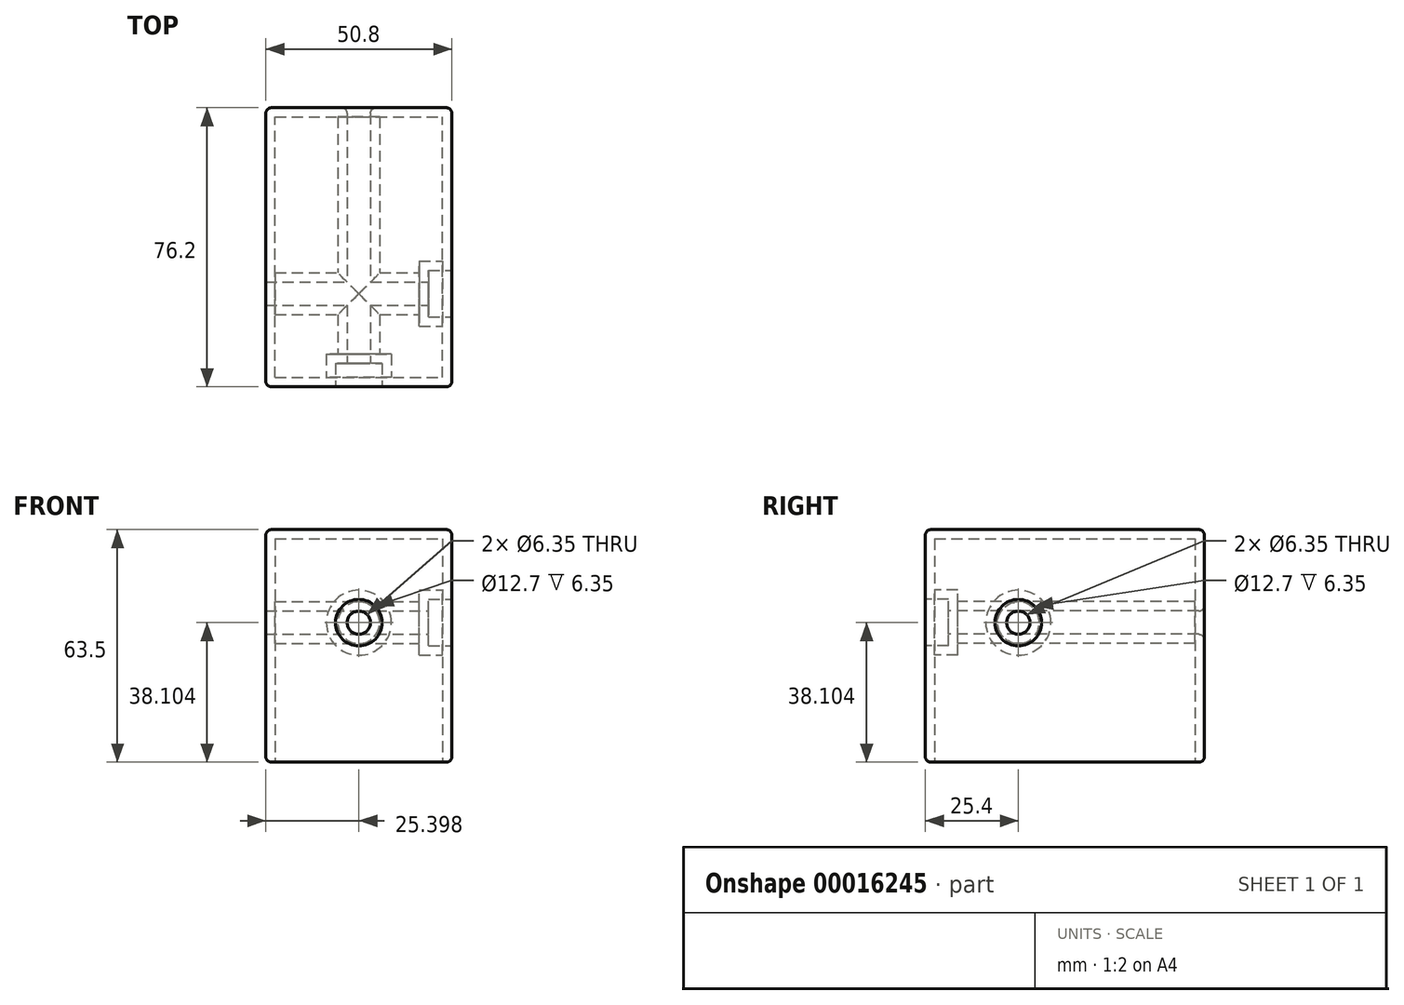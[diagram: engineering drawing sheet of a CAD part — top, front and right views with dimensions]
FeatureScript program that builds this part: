
annotation { "Feature Type Name" : "Feature", "Feature Type Description" : "" }
export const myFeature = defineFeature(function(context is Context, id is Id, definition is map)
    precondition{}
    {
        {
            var Q0;
            Q0=qCreatedBy(makeId("Front.planeOp"),FACE);
            var sketch = newSketch(context, id + "F0", { "sketchPlane" : qUnion([Q0])});
            skLineSegment(sketch, "E0.bottom", {"start": v(-45.47, 53.6) * mm, "end": v(5.33, 53.6) * mm});
            skLineSegment(sketch, "E0.top", {"start": v(-45.47, -9.9) * mm, "end": v(5.33, -9.9) * mm});
            skLineSegment(sketch, "E0.left", {"start": v(-45.47, 53.6) * mm, "end": v(-45.47, -9.9) * mm});
            skLineSegment(sketch, "E0.right", {"start": v(5.33, 53.6) * mm, "end": v(5.33, -9.9) * mm});
            skSolve(sketch);
        }
        {
            var Q0;
            Q0=makeQuery(id+"F0.imprint","IMPRINT",FACE,{"disambiguationData":[TD([[makeQuery(id+"F0.imprint","IMPRINT",EDGE,{"derivedFrom":sQuery(id+"F0.wireOp",EDGE,"E0.bottom")}),-1.0]])]});
            extrude(context, id + "F1", {"entities" : qUnion([Q0]), "depth" : 76.2 * mm});
        }
        {
            var Q0;
            Q0=makeQuery(id+"F1.opExtrude","CAP_FACE",FACE,{"disambiguationData":[OSD([sQuery(id+"F0.wireOp",EDGE,"E0.bottom"),sQuery(id+"F0.wireOp",EDGE,"E0.top"),sQuery(id+"F0.wireOp",EDGE,"E0.left"),sQuery(id+"F0.wireOp",EDGE,"E0.right")])],"isStart":false});
            var sketch = newSketch(context, id + "F2", { "sketchPlane" : qUnion([Q0])});
            skPoint(sketch, "E1", {"position": v(-20.07, 28.2) * mm});
            skSolve(sketch);
        }
        {
            var Q0;
            Q0=sQuery(id+"F2.wireOp",VERTEX,"E1");
            var Q1;
            Q1=makeQuery(id+"F1.opExtrude","SWEPT_BODY",BODY,{"disambiguationData":[OSD([sQuery(id+"F0.wireOp",EDGE,"E0.bottom"),sQuery(id+"F0.wireOp",EDGE,"E0.top"),sQuery(id+"F0.wireOp",EDGE,"E0.left"),sQuery(id+"F0.wireOp",EDGE,"E0.right")])]});
            hole(context, id + "F3", {"style" : HoleStyle.C_BORE, "holeDiameter" : 6.35 * mm, "cBoreDiameter" : 12.7 * mm, "cBoreDepth" : 6.35 * mm, "endStyle" : HoleEndStyle.THROUGH, "locations" : qUnion([Q0]), "scope" : qUnion([Q1])});
        }
        {
            var Q0;
            Q0=makeQuery(id+"F1.opExtrude","SWEPT_FACE",FACE,{"disambiguationData":[OSD([sQuery(id+"F0.wireOp",EDGE,"E0.right")])]});
            var sketch = newSketch(context, id + "F4", { "sketchPlane" : qUnion([Q0])});
            skCircle(sketch, "E2", {"center": v(-50.8, 28.2) * mm, "radius": 7.94 * mm});
            skSolve(sketch);
        }
        {
            var Q0;
            Q0=sQuery(id+"F4.wireOp",VERTEX,"E2.center");
            var Q1;
            Q1=makeQuery(id+"F1.opExtrude","SWEPT_BODY",BODY,{"disambiguationData":[OSD([sQuery(id+"F0.wireOp",EDGE,"E0.bottom"),sQuery(id+"F0.wireOp",EDGE,"E0.top"),sQuery(id+"F0.wireOp",EDGE,"E0.left"),sQuery(id+"F0.wireOp",EDGE,"E0.right")])]});
            hole(context, id + "F5", {"style" : HoleStyle.C_BORE, "holeDiameter" : 6.35 * mm, "cBoreDiameter" : 12.7 * mm, "cBoreDepth" : 6.35 * mm, "endStyle" : HoleEndStyle.THROUGH, "locations" : qUnion([Q0]), "scope" : qUnion([Q1])});
        }
        {
            var Q0;
            Q0=makeQuery(id+"F1.opExtrude","SWEPT_FACE",FACE,{"disambiguationData":[OSD([sQuery(id+"F0.wireOp",EDGE,"E0.top")])]});
            shell(context, id + "F6", {"entities" : qUnion([Q0]), "thickness" : 2.54 * mm});
        }
        {
            var Q0;
            Q0=makeQuery(id+"F1.opExtrude","SWEPT_EDGE",EDGE,{"disambiguationData":[OSD([sQuery(id+"F0.wireOp",EDGE,"E0.top"),sQuery(id+"F0.wireOp",EDGE,"E0.right")])]});
            var Q1;
            Q1=makeQuery(id+"F1.opExtrude","CAP_EDGE",EDGE,{"disambiguationData":[OSD([sQuery(id+"F0.wireOp",EDGE,"E0.right")])],"isStart":false});
            var Q2;
            Q2=makeQuery(id+"F1.opExtrude","CAP_EDGE",EDGE,{"disambiguationData":[OSD([sQuery(id+"F0.wireOp",EDGE,"E0.top")])],"isStart":false});
            var Q3;
            Q3=makeQuery(id+"F1.opExtrude","CAP_EDGE",EDGE,{"disambiguationData":[OSD([sQuery(id+"F0.wireOp",EDGE,"E0.left")])],"isStart":false});
            var Q4;
            Q4=makeQuery(id+"F1.opExtrude","SWEPT_EDGE",EDGE,{"disambiguationData":[OSD([sQuery(id+"F0.wireOp",EDGE,"E0.top"),sQuery(id+"F0.wireOp",EDGE,"E0.left")])]});
            var Q5;
            Q5=makeQuery(id+"F1.opExtrude","CAP_EDGE",EDGE,{"disambiguationData":[OSD([sQuery(id+"F0.wireOp",EDGE,"E0.top")])],"isStart":true});
            var Q6;
            Q6=makeQuery(id+"F1.opExtrude","SWEPT_EDGE",EDGE,{"disambiguationData":[OSD([sQuery(id+"F0.wireOp",EDGE,"E0.bottom"),sQuery(id+"F0.wireOp",EDGE,"E0.right")])]});
            var Q7;
            Q7=makeQuery(id+"F1.opExtrude","CAP_EDGE",EDGE,{"disambiguationData":[OSD([sQuery(id+"F0.wireOp",EDGE,"E0.bottom")])],"isStart":false});
            var Q8;
            Q8=makeQuery(id+"F1.opExtrude","SWEPT_EDGE",EDGE,{"disambiguationData":[OSD([sQuery(id+"F0.wireOp",EDGE,"E0.bottom"),sQuery(id+"F0.wireOp",EDGE,"E0.left")])]});
            var Q9;
            Q9=makeQuery(id+"F1.opExtrude","CAP_EDGE",EDGE,{"disambiguationData":[OSD([sQuery(id+"F0.wireOp",EDGE,"E0.bottom")])],"isStart":true});
            var Q10;
            Q10=makeQuery(id+"F1.opExtrude","CAP_EDGE",EDGE,{"disambiguationData":[OSD([sQuery(id+"F0.wireOp",EDGE,"E0.right")])],"isStart":true});
            var Q11;
            Q11=makeQuery(id+"F1.opExtrude","CAP_FACE",FACE,{"disambiguationData":[OSD([sQuery(id+"F0.wireOp",EDGE,"E0.bottom"),sQuery(id+"F0.wireOp",EDGE,"E0.top"),sQuery(id+"F0.wireOp",EDGE,"E0.left"),sQuery(id+"F0.wireOp",EDGE,"E0.right")])],"isStart":true});
            fillet(context, id + "F7", {"entities" : qUnion([Q0, Q1, Q2, Q3, Q4, Q5, Q6, Q7, Q8, Q9, Q10, Q11]), "radius" : 1.52 * mm, "tangentPropagation" : true, "allowEdgeOverflow" : false});
        }
    });
